# Revit family: Seating_Inc-Seat_Medium_Back-Cobra-1
name_source: partatom
category: Furniture
revit_build: Autodesk Revit 2014 (Build: 20130308_1515(x64)
units: mm (PartAtom-declared; Revit-internal decimal feet)

## types (1)
- Type Catalog
    Arm = 23"
    Arm Left = No
    Arm Metal Finish = STI - Power Coat, Black
    Arm Plastic Finish = STI - Plastic Black
    Arm Right = No
    Assembly Code = E2020200
    Back Finish = STI - Upholstery Latex
    Depth = 25"
    Description = Black Armless
    Glide Finish = STI - Plastic Black
    Height = 34"
    Keynote = 12500
    Leg Finish = STI - Power Coat, Black
    Low Emitting Finish = Yes
    Low Emitting Material = Yes
    Manufacturer = Seating Inc
    Model = CM443-21B
    Percentage of Recycled Content = 0
    Salvage or Reuse = Yes
    Seat Finish = STI - Upholstery Latex
    Support Finish = STI - Power Coat, Black
    Type Comments = Cobra Tandem Seating
    URL = www.seatinginc.com
    Width = 23"

## geometry (parser evidence)
native form markers: Sweep x4
no freeform markers — native parametric forms only
